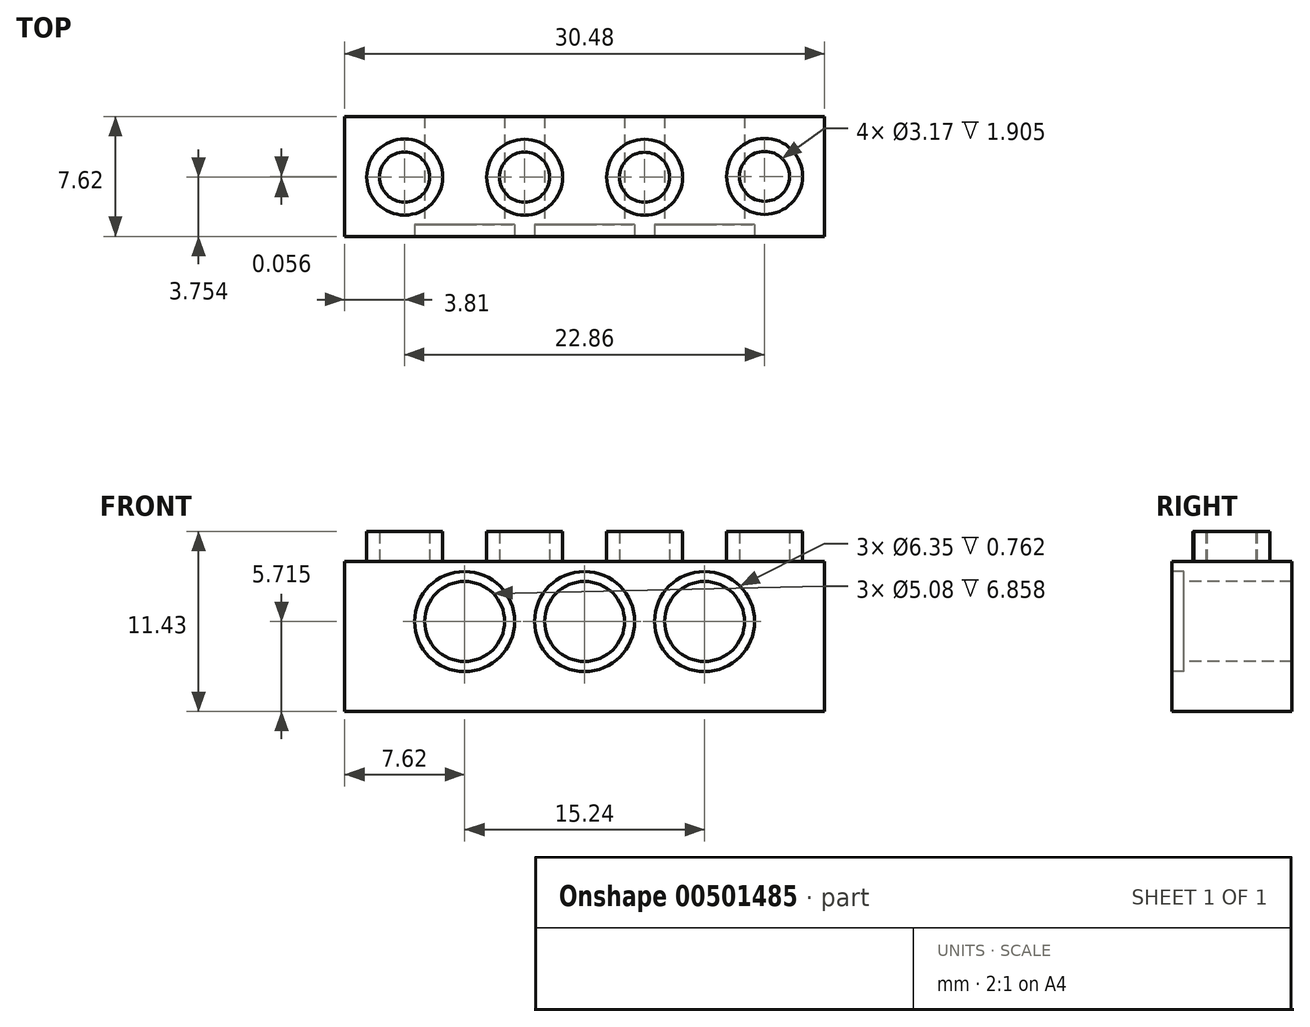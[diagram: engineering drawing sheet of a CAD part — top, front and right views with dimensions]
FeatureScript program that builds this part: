
annotation { "Feature Type Name" : "Feature", "Feature Type Description" : "" }
export const myFeature = defineFeature(function(context is Context, id is Id, definition is map)
    precondition{}
    {
        {
            var Q0;
            Q0=qCreatedBy(makeId("Front.planeOp"),FACE);
            var sketch = newSketch(context, id + "F0", { "sketchPlane" : qUnion([Q0])});
            skLineSegment(sketch, "E0", {"start": v(0, 9.52) * mm, "end": v(0, 0) * mm});
            skLineSegment(sketch, "E1", {"start": v(0, 9.52) * mm, "end": v(30.48, 9.53) * mm});
            skLineSegment(sketch, "E2", {"start": v(30.48, 9.53) * mm, "end": v(30.48, 0) * mm});
            skLineSegment(sketch, "E3", {"start": v(30.48, 0) * mm, "end": v(0, 0) * mm});
            skSolve(sketch);
        }
        {
            var Q0;
            Q0=makeQuery(id+"F0.imprint","IMPRINT",FACE,{"disambiguationData":[TD([[makeQuery(id+"F0.imprint","IMPRINT",EDGE,{"derivedFrom":sQuery(id+"F0.wireOp",EDGE,"E0")}),1.0]])]});
            extrude(context, id + "F1", {"entities" : qUnion([Q0]), "oppositeDirection" : true, "depth" : 7.62 * mm});
        }
        {
            var Q0;
            Q0=makeQuery(id+"F1.opExtrude","CAP_FACE",FACE,{"disambiguationData":[OSD([sQuery(id+"F0.wireOp",EDGE,"E0"),sQuery(id+"F0.wireOp",EDGE,"E1"),sQuery(id+"F0.wireOp",EDGE,"E2"),sQuery(id+"F0.wireOp",EDGE,"E3")])],"isStart":true});
            var sketch = newSketch(context, id + "F2", { "sketchPlane" : qUnion([Q0])});
            skCircle(sketch, "E4", {"center": v(15.24, 5.72) * mm, "radius": 3.18 * mm});
            skCircle(sketch, "E5", {"center": v(15.24, 5.72) * mm, "radius": 2.54 * mm});
            skCircle(sketch, "E6", {"center": v(7.62, 5.72) * mm, "radius": 3.18 * mm});
            skCircle(sketch, "E7", {"center": v(7.62, 5.72) * mm, "radius": 2.54 * mm});
            skCircle(sketch, "E8", {"center": v(22.86, 5.72) * mm, "radius": 3.18 * mm});
            skCircle(sketch, "E9", {"center": v(22.86, 5.72) * mm, "radius": 2.54 * mm});
            skSolve(sketch);
        }
        {
            var Q0;
            Q0=makeQuery(id+"F2.imprint","IMPRINT",FACE,{"disambiguationData":[TD([[makeQuery(id+"F2.imprint","IMPRINT",EDGE,{"derivedFrom":sQuery(id+"F2.wireOp",EDGE,"E6")}),1.0]])]});
            var Q1;
            Q1=makeQuery(id+"F2.imprint","IMPRINT",FACE,{"disambiguationData":[TD([[makeQuery(id+"F2.imprint","IMPRINT",EDGE,{"derivedFrom":sQuery(id+"F2.wireOp",EDGE,"E4")}),1.0]])]});
            var Q2;
            Q2=makeQuery(id+"F2.imprint","IMPRINT",FACE,{"disambiguationData":[TD([[makeQuery(id+"F2.imprint","IMPRINT",EDGE,{"derivedFrom":sQuery(id+"F2.wireOp",EDGE,"E8")}),1.0]])]});
            extrude(context, id + "F3", {"entities" : qUnion([Q0, Q1, Q2]), "operationType" : NewBodyOperationType.REMOVE, "oppositeDirection" : true, "depth" : 0.76 * mm});
        }
        {
            var Q0;
            Q0=makeQuery(id+"F3.boolean.opBoolean","SPLIT",FACE,{"disambiguationData":[TD([makeQuery(id+"F3.opExtrude","SWEPT_FACE",FACE,{"disambiguationData":[OSD([sQuery(id+"F2.wireOp",EDGE,"E7")])]})])],"derivedFrom":makeQuery(id+"F1.opExtrude","CAP_FACE",FACE,{"disambiguationData":[OSD([sQuery(id+"F0.wireOp",EDGE,"E0"),sQuery(id+"F0.wireOp",EDGE,"E1"),sQuery(id+"F0.wireOp",EDGE,"E2"),sQuery(id+"F0.wireOp",EDGE,"E3")])],"isStart":true})});
            var Q1;
            Q1=makeQuery(id+"F3.boolean.opBoolean","SPLIT",FACE,{"disambiguationData":[TD([makeQuery(id+"F3.opExtrude","SWEPT_FACE",FACE,{"disambiguationData":[OSD([sQuery(id+"F2.wireOp",EDGE,"E5")])]})])],"derivedFrom":makeQuery(id+"F1.opExtrude","CAP_FACE",FACE,{"disambiguationData":[OSD([sQuery(id+"F0.wireOp",EDGE,"E0"),sQuery(id+"F0.wireOp",EDGE,"E1"),sQuery(id+"F0.wireOp",EDGE,"E2"),sQuery(id+"F0.wireOp",EDGE,"E3")])],"isStart":true})});
            var Q2;
            Q2=makeQuery(id+"F3.boolean.opBoolean","SPLIT",FACE,{"disambiguationData":[TD([makeQuery(id+"F3.opExtrude","SWEPT_FACE",FACE,{"disambiguationData":[OSD([sQuery(id+"F2.wireOp",EDGE,"E9")])]})])],"derivedFrom":makeQuery(id+"F1.opExtrude","CAP_FACE",FACE,{"disambiguationData":[OSD([sQuery(id+"F0.wireOp",EDGE,"E0"),sQuery(id+"F0.wireOp",EDGE,"E1"),sQuery(id+"F0.wireOp",EDGE,"E2"),sQuery(id+"F0.wireOp",EDGE,"E3")])],"isStart":true})});
            extrude(context, id + "F4", {"entities" : qUnion([Q0, Q1, Q2]), "operationType" : NewBodyOperationType.REMOVE, "oppositeDirection" : true, "depth" : 10.16 * mm});
        }
        {
            var Q0;
            Q0=makeQuery(id+"F1.opExtrude","SWEPT_FACE",FACE,{"disambiguationData":[OSD([sQuery(id+"F0.wireOp",EDGE,"E1")])]});
            var sketch = newSketch(context, id + "F5", { "sketchPlane" : qUnion([Q0])});
            skCircle(sketch, "E10", {"center": v(26.67, 3.81) * mm, "radius": 2.41 * mm});
            skCircle(sketch, "E11", {"center": v(26.67, 3.81) * mm, "radius": 1.59 * mm});
            skCircle(sketch, "E12", {"center": v(3.81, 3.76) * mm, "radius": 2.41 * mm});
            skCircle(sketch, "E13", {"center": v(3.81, 3.76) * mm, "radius": 1.59 * mm});
            skCircle(sketch, "E14.1.0.0", {"center": v(11.43, 3.76) * mm, "radius": 1.59 * mm});
            skCircle(sketch, "E14.1.0.1", {"center": v(11.43, 3.76) * mm, "radius": 2.41 * mm});
            skCircle(sketch, "E14.2.0.0", {"center": v(19.05, 3.75) * mm, "radius": 1.59 * mm});
            skCircle(sketch, "E14.2.0.1", {"center": v(19.05, 3.75) * mm, "radius": 2.41 * mm});
            skLineSegment(sketch, "E14.direction1", {"start": v(3.8, 3.76) * mm, "end": v(11.43, 3.76) * mm, "construction": true});
            skSolve(sketch);
        }
        {
            var Q0;
            Q0=makeQuery(id+"F5.imprint","IMPRINT",FACE,{"disambiguationData":[TD([[makeQuery(id+"F5.imprint","IMPRINT",EDGE,{"derivedFrom":sQuery(id+"F5.wireOp",EDGE,"E12")}),1.0]])]});
            var Q1;
            Q1=makeQuery(id+"F5.imprint","IMPRINT",FACE,{"disambiguationData":[TD([[makeQuery(id+"F5.imprint","IMPRINT",EDGE,{"derivedFrom":sQuery(id+"F5.wireOp",EDGE,"E14.1.0.0")}),-1.0]])]});
            var Q2;
            Q2=makeQuery(id+"F5.imprint","IMPRINT",FACE,{"disambiguationData":[TD([[makeQuery(id+"F5.imprint","IMPRINT",EDGE,{"derivedFrom":sQuery(id+"F5.wireOp",EDGE,"E14.2.0.0")}),-1.0]])]});
            var Q3;
            Q3=makeQuery(id+"F5.imprint","IMPRINT",FACE,{"disambiguationData":[TD([[makeQuery(id+"F5.imprint","IMPRINT",EDGE,{"derivedFrom":sQuery(id+"F5.wireOp",EDGE,"E10")}),1.0]])]});
            extrude(context, id + "F6", {"entities" : qUnion([Q0, Q1, Q2, Q3]), "operationType" : NewBodyOperationType.ADD, "depth" : 1.9 * mm});
        }
    });
